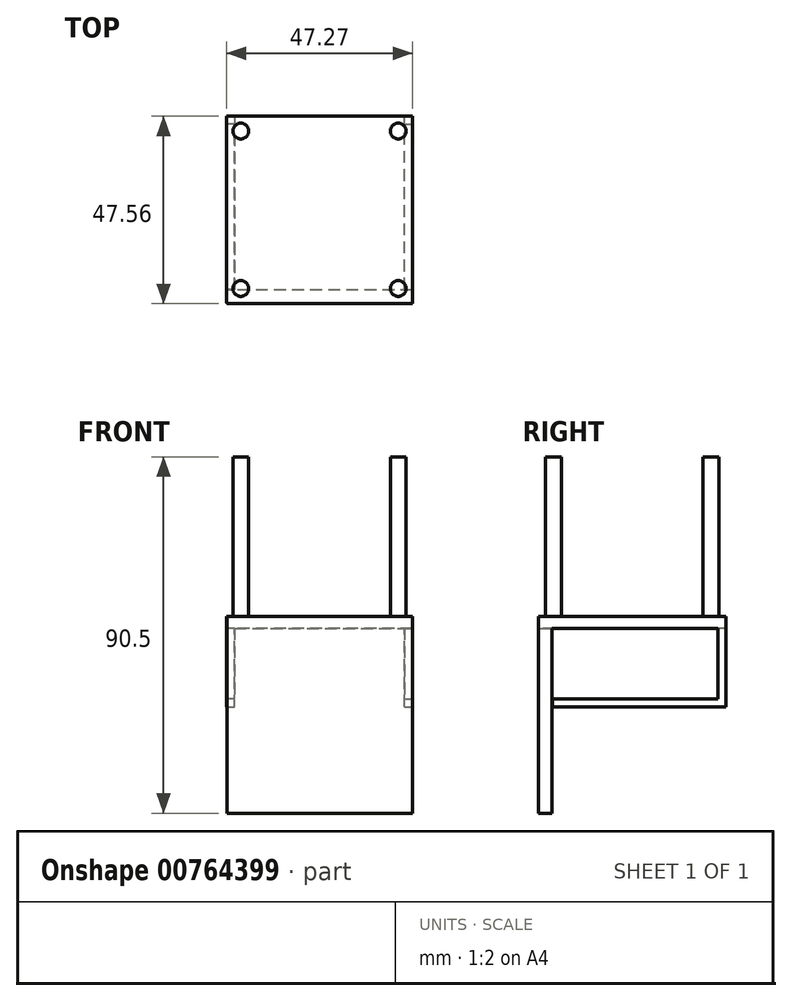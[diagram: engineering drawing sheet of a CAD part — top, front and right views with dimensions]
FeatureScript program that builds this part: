
annotation { "Feature Type Name" : "Feature", "Feature Type Description" : "" }
export const myFeature = defineFeature(function(context is Context, id is Id, definition is map)
    precondition{}
    {
        {
            var Q0;
            Q0=qCreatedBy(makeId("Top.planeOp"),FACE);
            var sketch = newSketch(context, id + "F0", { "sketchPlane" : qUnion([Q0])});
            skLineSegment(sketch, "E0.bottom", {"start": v(-19.13, 18.05) * mm, "end": v(20.87, 18.05) * mm, "construction": true});
            skLineSegment(sketch, "E0.top", {"start": v(-19.13, -21.95) * mm, "end": v(20.87, -21.95) * mm, "construction": true});
            skLineSegment(sketch, "E0.left", {"start": v(-19.13, 18.05) * mm, "end": v(-19.13, -21.95) * mm, "construction": true});
            skLineSegment(sketch, "E0.right", {"start": v(20.87, 18.05) * mm, "end": v(20.87, -21.95) * mm, "construction": true});
            skCircle(sketch, "E1", {"center": v(-19.13, 18.05) * mm, "radius": 2 * mm});
            skCircle(sketch, "E2", {"center": v(-19.13, -21.95) * mm, "radius": 2 * mm});
            skCircle(sketch, "E3", {"center": v(20.87, 18.05) * mm, "radius": 2 * mm});
            skCircle(sketch, "E4", {"center": v(20.87, -21.95) * mm, "radius": 2 * mm});
            skSolve(sketch);
        }
        {
            var Q0;
            Q0=makeQuery(id+"F0.imprint","IMPRINT",FACE,{"disambiguationData":[TD([[makeQuery(id+"F0.imprint","IMPRINT",EDGE,{"derivedFrom":sQuery(id+"F0.wireOp",EDGE,"E2")}),1.0]])]});
            var Q1;
            Q1=makeQuery(id+"F0.imprint","IMPRINT",FACE,{"disambiguationData":[TD([[makeQuery(id+"F0.imprint","IMPRINT",EDGE,{"derivedFrom":sQuery(id+"F0.wireOp",EDGE,"E3")}),1.0]])]});
            var Q2;
            Q2=makeQuery(id+"F0.imprint","IMPRINT",FACE,{"disambiguationData":[TD([[makeQuery(id+"F0.imprint","IMPRINT",EDGE,{"derivedFrom":sQuery(id+"F0.wireOp",EDGE,"E4")}),1.0]])]});
            var Q3;
            Q3=makeQuery(id+"F0.imprint","IMPRINT",FACE,{"disambiguationData":[TD([[makeQuery(id+"F0.imprint","IMPRINT",EDGE,{"derivedFrom":sQuery(id+"F0.wireOp",EDGE,"E1")}),1.0]])]});
            extrude(context, id + "F1", {"entities" : qUnion([Q0, Q1, Q2, Q3]), "depth" : 40.5 * mm, "offsetDistance" : 25 * mm});
        }
        {
            var Q0;
            Q0=qCreatedBy(makeId("Top.planeOp"),FACE);
            var sketch = newSketch(context, id + "F2", { "sketchPlane" : qUnion([Q0])});
            skLineSegment(sketch, "E5.bottom", {"start": v(-22.76, 21.8) * mm, "end": v(24.5, 21.8) * mm});
            skLineSegment(sketch, "E5.top", {"start": v(-22.76, -25.63) * mm, "end": v(24.5, -25.63) * mm});
            skLineSegment(sketch, "E5.left", {"start": v(-22.76, 21.8) * mm, "end": v(-22.76, -25.63) * mm});
            skLineSegment(sketch, "E5.right", {"start": v(24.5, 21.8) * mm, "end": v(24.5, -25.63) * mm});
            skSolve(sketch);
        }
        {
            var Q0;
            Q0 = qSketchRegion(id + "F2", true);
            extrude(context, id + "F3", {"entities" : qUnion([Q0]), "operationType" : NewBodyOperationType.ADD, "oppositeDirection" : true, "depth" : 3 * mm, "offsetDistance" : 25 * mm});
        }
        {
            var Q0;
            Q0=qCreatedBy(makeId("Top.planeOp"),FACE);
            var sketch = newSketch(context, id + "F4", { "sketchPlane" : qUnion([Q0])});
            skLineSegment(sketch, "E6.bottom", {"start": v(24.5, -25.77) * mm, "end": v(-22.61, -25.77) * mm});
            skLineSegment(sketch, "E6.top", {"start": v(24.5, -22.35) * mm, "end": v(-22.61, -22.35) * mm});
            skLineSegment(sketch, "E6.left", {"start": v(24.5, -25.77) * mm, "end": v(24.5, -22.35) * mm});
            skLineSegment(sketch, "E6.right", {"start": v(-22.61, -25.77) * mm, "end": v(-22.61, -22.35) * mm});
            skSolve(sketch);
        }
        {
            var Q0;
            Q0 = qSketchRegion(id + "F4", true);
            extrude(context, id + "F5", {"entities" : qUnion([Q0]), "operationType" : NewBodyOperationType.ADD, "oppositeDirection" : true, "depth" : 50 * mm, "offsetDistance" : 25 * mm});
        }
        {
            var Q0;
            Q0=makeQuery(id+"F3.opExtrude","CAP_FACE",FACE,{"disambiguationData":[OSD([sQuery(id+"F2.wireOp",EDGE,"E5.bottom"),sQuery(id+"F2.wireOp",EDGE,"E5.top"),sQuery(id+"F2.wireOp",EDGE,"E5.left"),sQuery(id+"F2.wireOp",EDGE,"E5.right")])],"isStart":false});
            var sketch = newSketch(context, id + "F6", { "sketchPlane" : qUnion([Q0])});
            skLineSegment(sketch, "E7.bottom", {"start": v(22.5, 22.2) * mm, "end": v(24.5, 22.2) * mm});
            skLineSegment(sketch, "E7.top", {"start": v(22.5, -21.8) * mm, "end": v(24.5, -21.8) * mm});
            skLineSegment(sketch, "E7.left", {"start": v(22.5, 22.2) * mm, "end": v(22.5, -21.8) * mm});
            skLineSegment(sketch, "E7.right", {"start": v(24.5, 22.2) * mm, "end": v(24.5, -21.8) * mm});
            skSolve(sketch);
        }
        {
            var Q0;
            Q0 = qSketchRegion(id + "F6", true);
            extrude(context, id + "F7", {"entities" : qUnion([Q0]), "operationType" : NewBodyOperationType.ADD, "depth" : 20 * mm, "offsetDistance" : 25 * mm});
        }
        {
            var Q0;
            Q0=makeQuery(id+"F3.opExtrude","CAP_FACE",FACE,{"disambiguationData":[OSD([sQuery(id+"F2.wireOp",EDGE,"E5.bottom"),sQuery(id+"F2.wireOp",EDGE,"E5.top"),sQuery(id+"F2.wireOp",EDGE,"E5.left"),sQuery(id+"F2.wireOp",EDGE,"E5.right")])],"isStart":false});
            var sketch = newSketch(context, id + "F8", { "sketchPlane" : qUnion([Q0])});
            skLineSegment(sketch, "E8.bottom", {"start": v(-22.76, -21.8) * mm, "end": v(-20.76, -21.8) * mm});
            skLineSegment(sketch, "E8.top", {"start": v(-22.76, 22.2) * mm, "end": v(-20.76, 22.2) * mm});
            skLineSegment(sketch, "E8.left", {"start": v(-22.76, -21.8) * mm, "end": v(-22.76, 22.2) * mm});
            skLineSegment(sketch, "E8.right", {"start": v(-20.76, -21.8) * mm, "end": v(-20.76, 22.2) * mm});
            skSolve(sketch);
        }
        {
            var Q0;
            Q0 = qSketchRegion(id + "F8", true);
            extrude(context, id + "F9", {"entities" : qUnion([Q0]), "operationType" : NewBodyOperationType.ADD, "depth" : 20 * mm, "offsetDistance" : 25 * mm});
        }
        {
            var Q0;
            Q0=makeQuery(id+"F7.boolean.opBoolean","MERGE",FACE,{"derivedFrom":[makeQuery(id+"F3.opExtrude","SWEPT_FACE",FACE,{"disambiguationData":[OSD([sQuery(id+"F2.wireOp",EDGE,"E5.right")])]}),makeQuery(id+"F7.opExtrude","SWEPT_FACE",FACE,{"disambiguationData":[OSD([sQuery(id+"F6.wireOp",EDGE,"E7.right")])]})]});
            var sketch = newSketch(context, id + "F10", { "sketchPlane" : qUnion([Q0])});
            skLineSegment(sketch, "E9.bottom", {"start": v(-22.2, -3) * mm, "end": v(19.8, -3) * mm});
            skLineSegment(sketch, "E9.top", {"start": v(-22.2, -21) * mm, "end": v(19.8, -21) * mm});
            skLineSegment(sketch, "E9.left", {"start": v(-22.2, -3) * mm, "end": v(-22.2, -21) * mm});
            skLineSegment(sketch, "E9.right", {"start": v(19.8, -3) * mm, "end": v(19.8, -21) * mm});
            skSolve(sketch);
        }
        {
            var Q0;
            Q0 = qSketchRegion(id + "F10", true);
            extrude(context, id + "F11", {"entities" : qUnion([Q0]), "operationType" : NewBodyOperationType.REMOVE, "oppositeDirection" : true, "depth" : 25 * mm, "offsetDistance" : 25 * mm});
        }
        {
            var Q0;
            Q0=makeQuery(id+"F9.boolean.opBoolean","MERGE",FACE,{"derivedFrom":[makeQuery(id+"F3.opExtrude","SWEPT_FACE",FACE,{"disambiguationData":[OSD([sQuery(id+"F2.wireOp",EDGE,"E5.left")])]}),makeQuery(id+"F9.opExtrude","SWEPT_FACE",FACE,{"disambiguationData":[OSD([sQuery(id+"F8.wireOp",EDGE,"E8.left")])]})]});
            var sketch = newSketch(context, id + "F12", { "sketchPlane" : qUnion([Q0])});
            skLineSegment(sketch, "E10.bottom", {"start": v(22.2, -3) * mm, "end": v(-19.8, -3) * mm});
            skLineSegment(sketch, "E10.top", {"start": v(22.2, -21) * mm, "end": v(-19.8, -21) * mm});
            skLineSegment(sketch, "E10.left", {"start": v(22.2, -3) * mm, "end": v(22.2, -21) * mm});
            skLineSegment(sketch, "E10.right", {"start": v(-19.8, -3) * mm, "end": v(-19.8, -21) * mm});
            skSolve(sketch);
        }
        {
            var Q0;
            Q0 = qSketchRegion(id + "F12", true);
            extrude(context, id + "F13", {"entities" : qUnion([Q0]), "operationType" : NewBodyOperationType.REMOVE, "oppositeDirection" : true, "depth" : 25 * mm, "offsetDistance" : 25 * mm});
        }
    });
